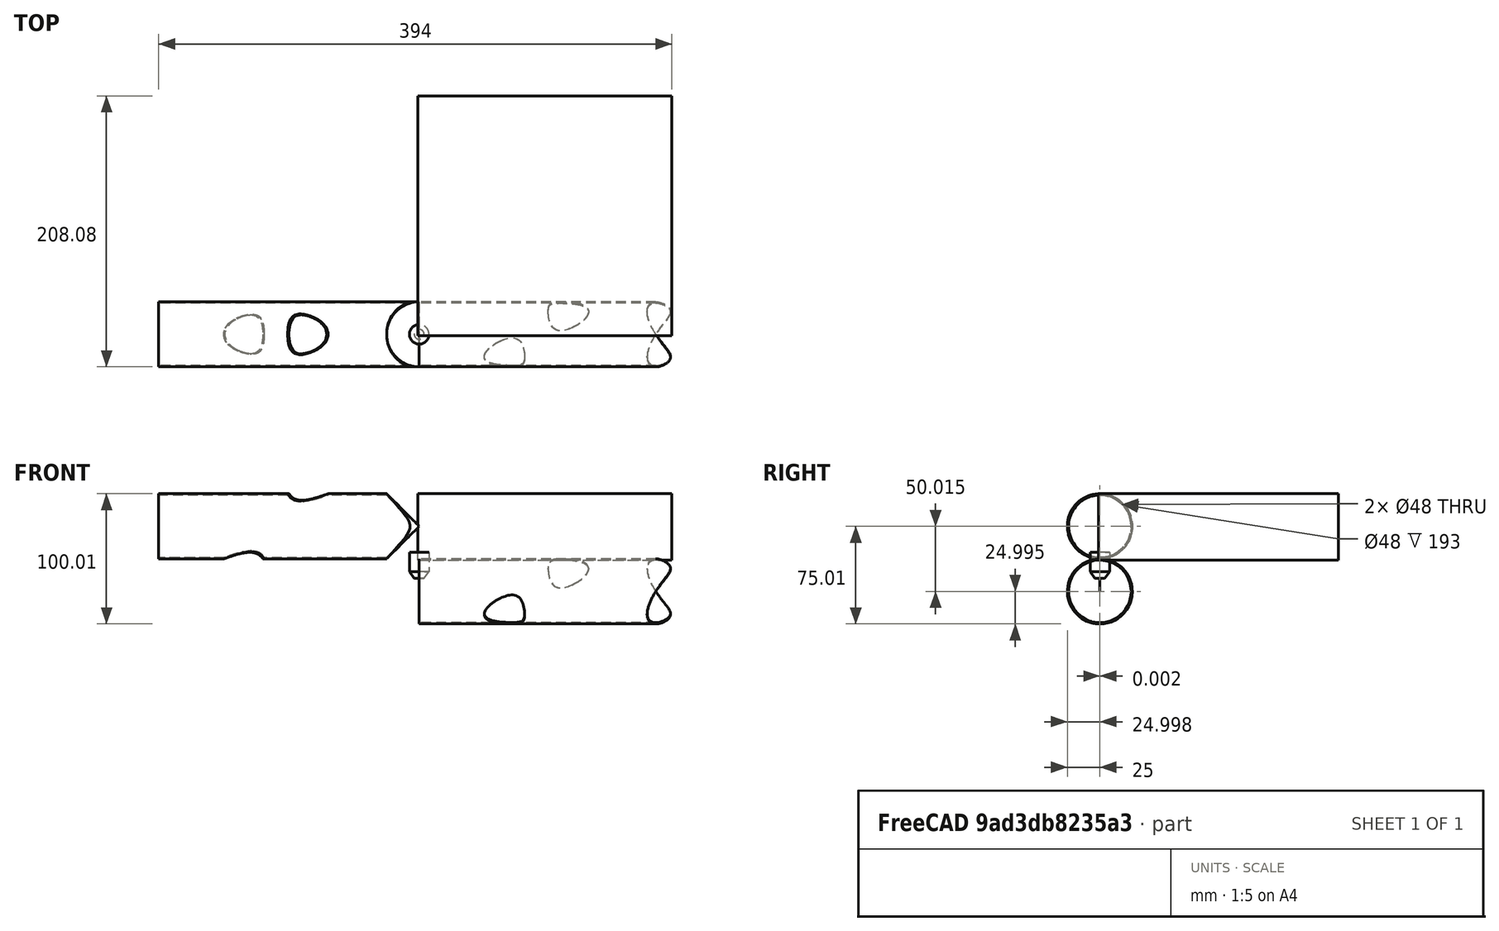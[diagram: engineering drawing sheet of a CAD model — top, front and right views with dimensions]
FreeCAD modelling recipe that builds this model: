
FCSTD DOCUMENT  (FreeCAD 0.20R25747 (Git))
Label: pipe_normalcut_path_axisMap
License: All rights reserved
LicenseURL: http://en.wikipedia.org/wiki/All_rights_reserved
objects: Part::FeaturePython×7, Path::FeaturePython×4, App::Link×3, App::DocumentObjectGroup×3, Part::Offset×2, Part::Feature×2, Part::Cylinder×1, Part::MultiCommon×1, App::FeaturePython×1, Path::FeatureCompoundPython×1
note: 13 computed .brp shape members not serialized (recipe doc carries the construction recipe); baked Part::Feature solids carry a one-line shape summary decoded from their .brp

FEATURE [Part::Cylinder] Cylinder
  Angle = 360
  AttacherType = Attacher::AttachEngine3D
  FirstAngle = 45
  Height = 80
  Placement = pos=(-150,0,10) rot=(0,0,1;0rad)
  Radius = 15
  SecondAngle = 0
FEATURE [Part::FeaturePython] Tube  # WARN: FeaturePython — macro-defined, semantics opaque (R4)
  AttacherType = Attacher::AttachEngine3D
  Height = 100
  InnerRadius = 24
  OuterRadius = 25
FEATURE [Part::FeaturePython] Tube001  # WARN: FeaturePython — macro-defined, semantics opaque (R4)
  AttacherType = Attacher::AttachEngine3D
  Height = 200
  InnerRadius = 24
  OuterRadius = 25
  Placement = pos=(0,0,50) rot=(0.357407,-0.862856,-0.357407;1.71777rad)
FEATURE [Part::FeaturePython] Cutout  # WARN: FeaturePython — macro-defined, semantics opaque (R4)
  Base = -> Tube001
  Tolerance = 0
  Tool = -> Tube
FEATURE [Part::FeaturePython] Cutout001  # WARN: FeaturePython — macro-defined, semantics opaque (R4)
  Base = -> Cutout
  Tolerance = 0
  Tool = -> Cylinder
FEATURE [App::Link] Link  label="Cutout002"
  LinkTransform = true
  LinkedObject = -> Cutout001 [Face1]
FEATURE [App::Link] Link001  label="Cutout003"
  LinkTransform = true
  LinkedObject = -> Cutout001 [Face6]
FEATURE [Part::Offset] Offset
  Fill = true
  Intersection = false
  Join = 0
  Mode = 0
  SelfIntersection = false
  Source = -> Link
  Value = -1
FEATURE [Part::Offset] Offset001
  Fill = true
  Intersection = false
  Join = 0
  Mode = 0
  SelfIntersection = false
  Source = -> Link001
  Value = -1
FEATURE [Part::MultiCommon] Common
  Shapes = -> [Offset,Offset001]
FEATURE [App::DocumentObjectGroup] Group  label="Model"
  Group = -> [Cutout001,Common]
FEATURE [Part::Feature] Common001  label="RotatedAndTranslatedCopy"
  Placement = pos=(200,-35.357,-35.37) rot=(-1,0,0;0.785398rad)
  shape: bbox 193 x 67.04 x 62.1 mm, 12 faces (baked)
FEATURE [Part::Feature] Shape
  shape: bbox 193 x 157.1 x 2.027e-07 mm, 0 faces, 0 solids (baked)
FEATURE [App::Link] Link002  label="RotatedAndTranslatedCopy001"
  LinkTransform = true
  LinkedObject = -> Common001
FEATURE [App::FeaturePython] SetupSheet  # Path/CAM operation (typed FeaturePython)
  ClearanceHeightExpression = OpStockZMax+SetupSheet.ClearanceHeightOffset
  ClearanceHeightOffset = 5
  CoolantMode = 0
  CoolantModes = None | Flood | Mist
  FinalDepthExpression = OpFinalDepth
  HorizRapid = 60000
  SafeHeightExpression = OpStockZMax+SetupSheet.SafeHeightOffset
  SafeHeightOffset = 3
  StartDepthExpression = OpStartDepth
  StepDownExpression = OpToolDiameter
  VertRapid = 60000
FEATURE [Part::FeaturePython] Clone  label="Model-Shape"  # Draft clone (typed FeaturePython)
  AttacherType = Attacher::AttachEngine3D
  Fuse = false
  Objects = -> [Shape]
  PathResource = Model
  Scale = (1,1,1)
FEATURE [App::DocumentObjectGroup] Model  label="Model001"
  Group = -> [Clone,Link002]
FEATURE [Part::FeaturePython] ToolBit  label="100um laser003"  # Path/CAM toolbit (typed FeaturePython)
  BitPropertyNames = Chipload | CuttingEdgeHeight | Diameter | Flutes | Length | Material | ShankDiameter
  BitShape = <userpath>/Documents/GitHub/FreeCADBuild/Mod\Path\Tools\Shape\laser.fcstd
  Chipload = 0
  CuttingEdgeHeight = 10
  Diameter = 0.1
  Flutes = 0
  Length = 30
  Material = 0
  ShankDiameter = 15
  ShapeName = laser
FEATURE [Path::FeaturePython] _00um_laser  label="100um laser001"  # Path/CAM operation (typed FeaturePython)
  HorizFeed = 10000
  HorizRapid = 60000
  SpindleDir = 0
  SpindleSpeed = 0
  Tool = -> ToolBit
  ToolNumber = 2
  VertFeed = 10000
  VertRapid = 60000
  expr: VertRapid = SetupSheet.VertRapid
  expr: HorizRapid = SetupSheet.HorizRapid
FEATURE [App::DocumentObjectGroup] Tools
  Group = -> [_00um_laser]
FEATURE [Part::FeaturePython] Stock  # WARN: FeaturePython — macro-defined, semantics opaque (R4)
  Base = -> Model
  ExtXneg = 1
  ExtXpos = 1
  ExtYneg = 1
  ExtYpos = 1
  ExtZneg = 1
  ExtZpos = 0
  Placement = pos=(0,-0.00166094,24.9853) rot=(0,0,1;0rad)
  StockType = FromBase
FEATURE [Path::FeaturePython] Engrave  # Path/CAM operation (typed FeaturePython)
  Active = true
  Base = -> [Clone]
  ClearanceHeight = 29.9853
  CoolantMode = None
  CycleTime = 00:00:00
  FinalDepth = 24.9853
  OpFinalDepth = 24.8853
  OpStartDepth = 24.9853
  OpStockZMax = 24.9853
  OpStockZMin = 23.9853
  OpToolDiameter = 0.1
  SafeHeight = 27.9853
  StartDepth = 24.9853
  StartVertex = 0
  StepDown = 0
  ToolController = -> _00um_laser
  expr: StartDepth = OpStartDepth
  expr: FinalDepth = OpStartDepth
  expr: SafeHeight = OpStockZMax + SetupSheet.SafeHeightOffset
  expr: ClearanceHeight = OpStockZMax + SetupSheet.ClearanceHeightOffset
FEATURE [Path::FeaturePython] AxisMapDressup  # Path/CAM operation (typed FeaturePython)
  AxisMap = 1
  Base = -> Engrave
  Radius = 24.99
FEATURE [Path::FeatureCompoundPython] Operations  # Path/CAM operation (typed FeaturePython)
  Group = -> [AxisMapDressup]
  UsePlacements = false
FEATURE [Path::FeaturePython] Job  # Path/CAM operation (typed FeaturePython)
  CycleTime = 00:00:00
  Fixtures = G54
  GeometryTolerance = 0.01
  Model = -> Model
  Operations = -> Operations
  OrderOutputBy = 0
  PostProcessor = 7
  SetupSheet = -> SetupSheet
  SplitOutput = false
  Stock = -> Stock
  Tools = -> Tools
